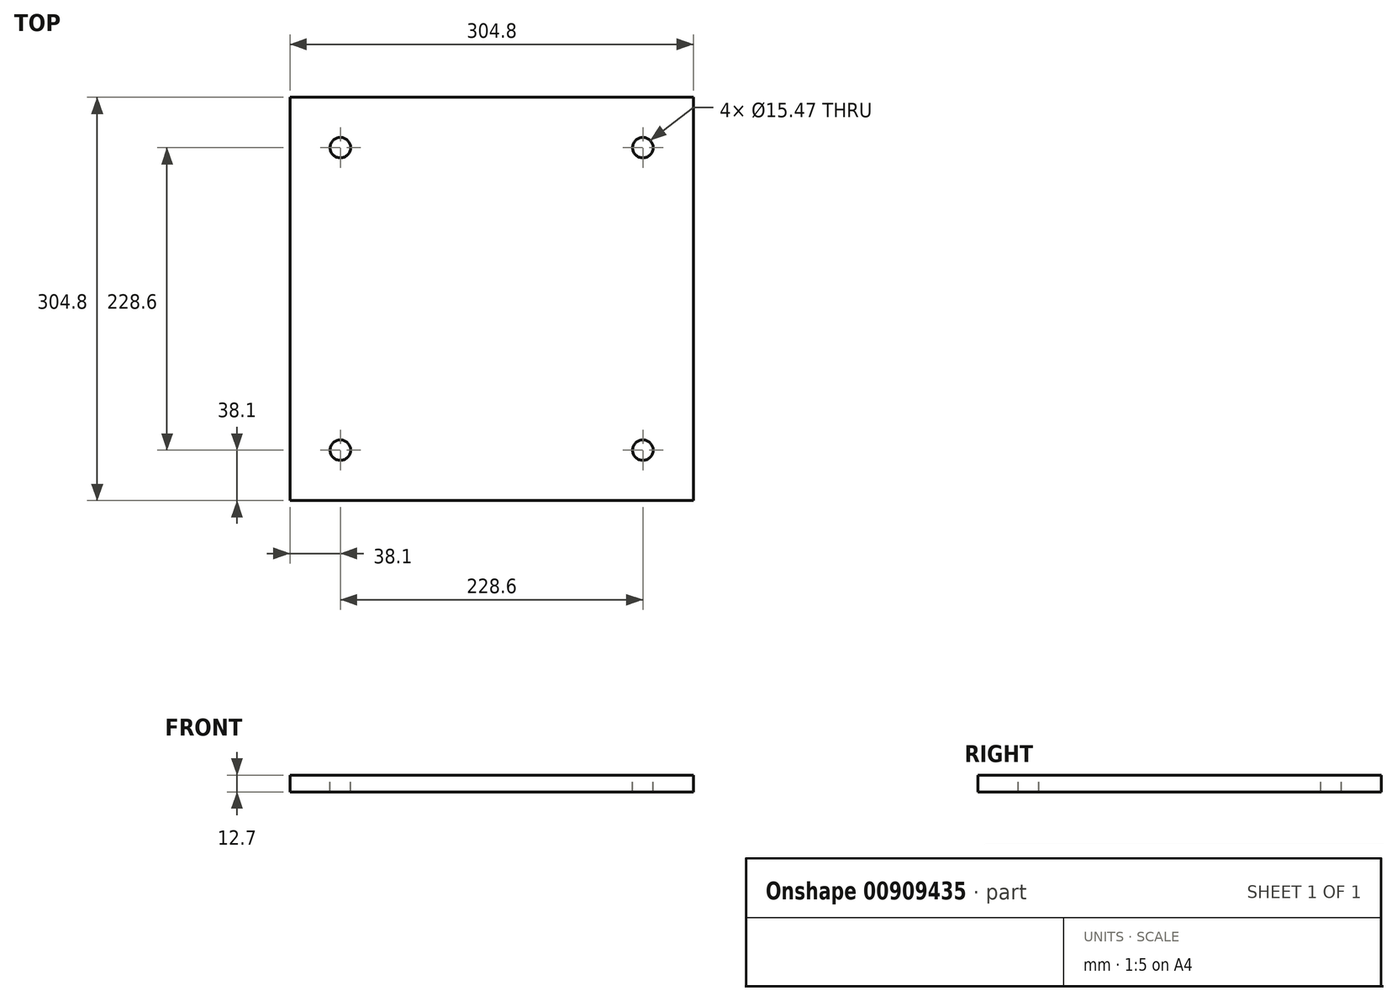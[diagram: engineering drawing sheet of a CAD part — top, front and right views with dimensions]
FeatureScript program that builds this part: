
annotation { "Feature Type Name" : "Feature", "Feature Type Description" : "" }
export const myFeature = defineFeature(function(context is Context, id is Id, definition is map)
    precondition{}
    {
        {
            var Q0;
            Q0=qCreatedBy(makeId("Top.planeOp"),FACE);
            var sketch = newSketch(context, id + "F0", { "sketchPlane" : qUnion([Q0])});
            skLineSegment(sketch, "E0.bottom", {"start": v(-152.4, 152.4) * mm, "end": v(152.4, 152.4) * mm});
            skLineSegment(sketch, "E0.top", {"start": v(-152.4, -152.4) * mm, "end": v(152.4, -152.4) * mm});
            skLineSegment(sketch, "E0.left", {"start": v(-152.4, 152.4) * mm, "end": v(-152.4, -152.4) * mm});
            skLineSegment(sketch, "E0.right", {"start": v(152.4, 152.4) * mm, "end": v(152.4, -152.4) * mm});
            skLineSegment(sketch, "E1", {"start": v(-152.4, 0) * mm, "end": v(0, 0) * mm, "construction": true});
            skLineSegment(sketch, "E2", {"start": v(0, 0) * mm, "end": v(0, 152.4) * mm, "construction": true});
            skSolve(sketch);
        }
        {
            var Q0;
            Q0 = qSketchRegion(id + "F0", true);
            extrude(context, id + "F1", {"entities" : qUnion([Q0]), "depth" : 12.7 * mm, "offsetDistance" : 25.4 * mm});
        }
        {
            var Q0;
            Q0=makeQuery(id+"F1.opExtrude","CAP_FACE",FACE,{"disambiguationData":[OSD([sQuery(id+"F0.wireOp",EDGE,"E0.bottom"),sQuery(id+"F0.wireOp",EDGE,"E0.top"),sQuery(id+"F0.wireOp",EDGE,"E0.left"),sQuery(id+"F0.wireOp",EDGE,"E0.right")])],"isStart":false});
            var sketch = newSketch(context, id + "F2", { "sketchPlane" : qUnion([Q0])});
            skLineSegment(sketch, "E3.bottom", {"start": v(-114.3, 114.3) * mm, "end": v(114.3, 114.3) * mm, "construction": true});
            skLineSegment(sketch, "E3.top", {"start": v(-114.3, -114.3) * mm, "end": v(114.3, -114.3) * mm, "construction": true});
            skLineSegment(sketch, "E3.left", {"start": v(-114.3, 114.3) * mm, "end": v(-114.3, -114.3) * mm, "construction": true});
            skLineSegment(sketch, "E3.right", {"start": v(114.3, 114.3) * mm, "end": v(114.3, -114.3) * mm, "construction": true});
            skLineSegment(sketch, "E4", {"start": v(114.3, 0) * mm, "end": v(0, 0) * mm, "construction": true});
            skLineSegment(sketch, "E5", {"start": v(0, 0) * mm, "end": v(0, 114.3) * mm, "construction": true});
            skSolve(sketch);
        }
        {
            var Q0;
            Q0=sQuery(id+"F2.wireOp",VERTEX,"E3.bottom.start");
            var Q1;
            Q1=sQuery(id+"F2.wireOp",VERTEX,"E3.bottom.end");
            var Q2;
            Q2=sQuery(id+"F2.wireOp",VERTEX,"E3.top.end");
            var Q3;
            Q3=sQuery(id+"F2.wireOp",VERTEX,"E3.top.start");
            var Q4;
            Q4=makeQuery(id+"F1.opExtrude","SWEPT_BODY",BODY,{"disambiguationData":[OSD([sQuery(id+"F0.wireOp",EDGE,"E0.bottom"),sQuery(id+"F0.wireOp",EDGE,"E0.top"),sQuery(id+"F0.wireOp",EDGE,"E0.left"),sQuery(id+"F0.wireOp",EDGE,"E0.right")])]});
            hole(context, id + "F3", {"style" : HoleStyle.SIMPLE, "endStyle" : HoleEndStyle.THROUGH, "standardTappedOrClearance" : lookupTablePath({ "fit" : "Loose (ASME)", "standard" : "ANSI", "size" : "1/2", "type" : "Clearance" }), "standardBlindInLast" : lookupTablePath({ "fit" : "Loose", "standard" : "ANSI", "size" : "1/2", "type" : "Clearance" }), "holeDiameter" : 15.47 * mm, "majorDiameter" : 6.35 * mm, "isTappedThrough" : true, "tappedDepth" : 12.7 * mm, "tapClearance" : 3, "locations" : qUnion([Q0, Q1, Q2, Q3]), "scope" : qUnion([Q4])});
        }
    });
